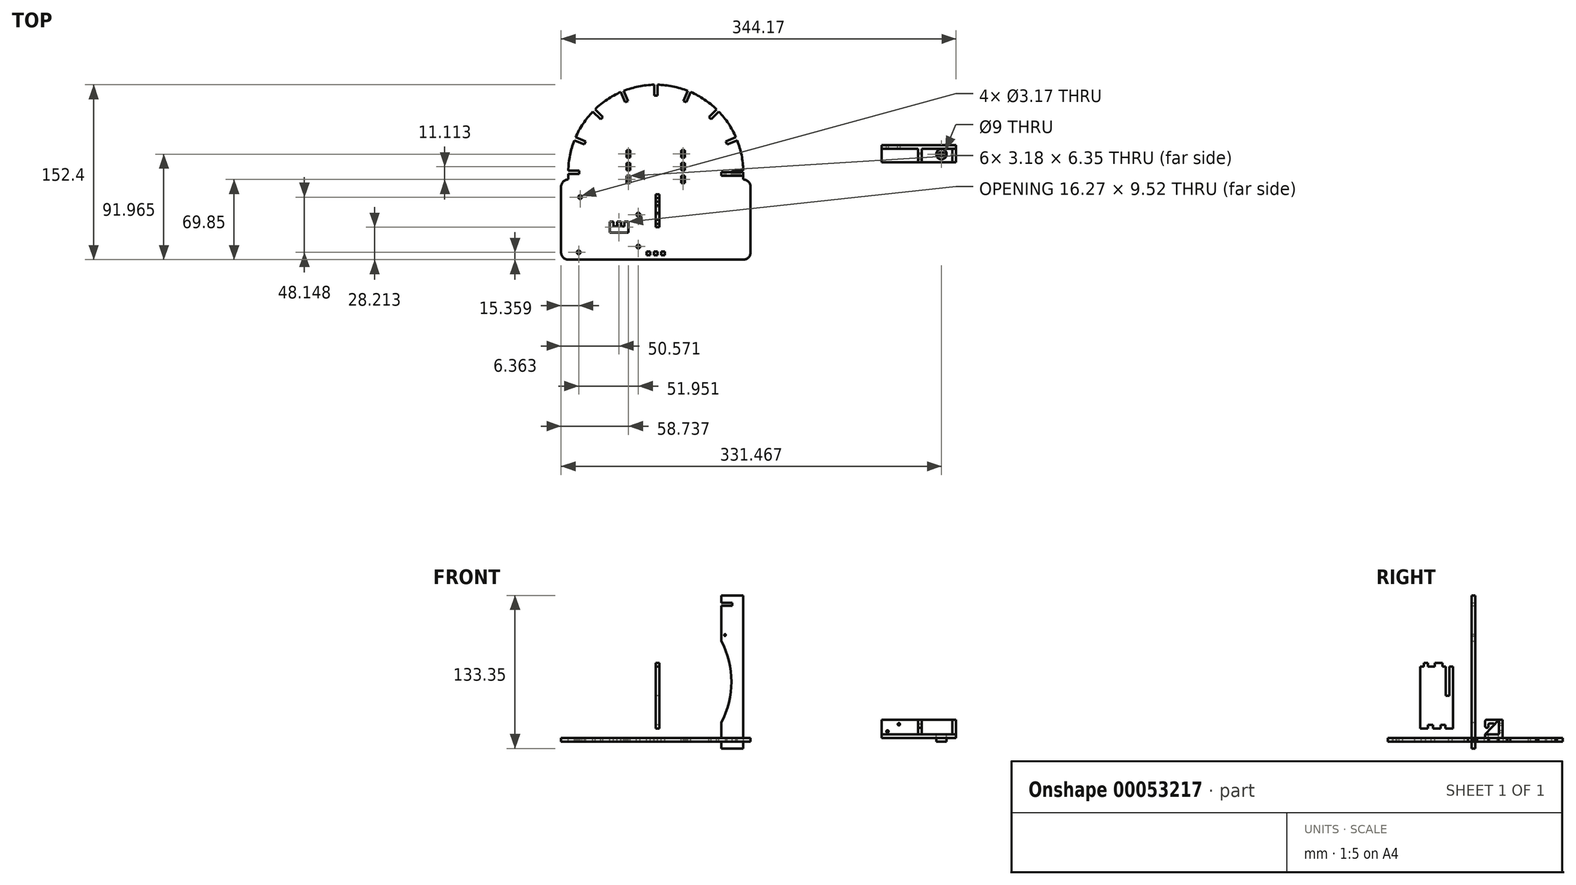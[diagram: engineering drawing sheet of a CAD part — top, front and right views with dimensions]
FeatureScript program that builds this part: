
annotation { "Feature Type Name" : "Feature", "Feature Type Description" : "" }
export const myFeature = defineFeature(function(context is Context, id is Id, definition is map)
    precondition{}
    {
        {
            var Q0;
            Q0=qCreatedBy(makeId("Top.planeOp"),FACE);
            var sketch = newSketch(context, id + "F0", { "sketchPlane" : qUnion([Q0])});
            skLineSegment(sketch, "E0", {"start": v(-76.2, -1.39) * mm, "end": v(-76.2, -6.35) * mm});
            skLineSegment(sketch, "E1", {"start": v(76.2, -1.39) * mm, "end": v(76.2, -6.35) * mm});
            skLineSegment(sketch, "E2.bottom", {"start": v(-66.67, -1.39) * mm, "end": v(-76.2, -1.39) * mm});
            skLineSegment(sketch, "E2.top", {"start": v(-66.67, 1.39) * mm, "end": v(-76.2, 1.39) * mm});
            skLineSegment(sketch, "E2.left", {"start": v(-66.67, -1.39) * mm, "end": v(-66.67, 1.39) * mm});
            skPoint(sketch, "E3", {"position": v(-76.2, 0) * mm});
            skLineSegment(sketch, "E4.1.0", {"start": v(-62.13, 24.23) * mm, "end": v(-70.93, 27.88) * mm});
            skLineSegment(sketch, "E4.1.1", {"start": v(-61.07, 26.8) * mm, "end": v(-69.87, 30.44) * mm});
            skLineSegment(sketch, "E4.1.2", {"start": v(-62.13, 24.23) * mm, "end": v(-61.07, 26.8) * mm});
            skLineSegment(sketch, "E4.2.0", {"start": v(-48.13, 46.16) * mm, "end": v(-54.86, 52.9) * mm});
            skLineSegment(sketch, "E4.2.1", {"start": v(-46.16, 48.13) * mm, "end": v(-52.9, 54.86) * mm});
            skLineSegment(sketch, "E4.2.2", {"start": v(-48.13, 46.16) * mm, "end": v(-46.16, 48.13) * mm});
            skLineSegment(sketch, "E4.3.0", {"start": v(-26.8, 61.07) * mm, "end": v(-30.44, 69.87) * mm});
            skLineSegment(sketch, "E4.3.1", {"start": v(-24.23, 62.13) * mm, "end": v(-27.88, 70.93) * mm});
            skLineSegment(sketch, "E4.3.2", {"start": v(-26.8, 61.07) * mm, "end": v(-24.23, 62.13) * mm});
            skLineSegment(sketch, "E4.4.0", {"start": v(-1.39, 66.67) * mm, "end": v(-1.39, 76.2) * mm});
            skLineSegment(sketch, "E4.4.1", {"start": v(1.39, 66.67) * mm, "end": v(1.39, 76.2) * mm});
            skLineSegment(sketch, "E4.4.2", {"start": v(-1.39, 66.67) * mm, "end": v(1.39, 66.67) * mm});
            skLineSegment(sketch, "E4.5.0", {"start": v(24.23, 62.13) * mm, "end": v(27.88, 70.93) * mm});
            skLineSegment(sketch, "E4.5.1", {"start": v(26.8, 61.07) * mm, "end": v(30.44, 69.87) * mm});
            skLineSegment(sketch, "E4.5.2", {"start": v(24.23, 62.13) * mm, "end": v(26.8, 61.07) * mm});
            skLineSegment(sketch, "E4.6.0", {"start": v(46.16, 48.13) * mm, "end": v(52.9, 54.86) * mm});
            skLineSegment(sketch, "E4.6.1", {"start": v(48.13, 46.16) * mm, "end": v(54.86, 52.9) * mm});
            skLineSegment(sketch, "E4.6.2", {"start": v(46.16, 48.13) * mm, "end": v(48.13, 46.16) * mm});
            skLineSegment(sketch, "E4.7.0", {"start": v(61.07, 26.8) * mm, "end": v(69.87, 30.44) * mm});
            skLineSegment(sketch, "E4.7.1", {"start": v(62.13, 24.23) * mm, "end": v(70.93, 27.88) * mm});
            skLineSegment(sketch, "E4.7.2", {"start": v(61.07, 26.8) * mm, "end": v(62.13, 24.23) * mm});
            skLineSegment(sketch, "E4.8.0", {"start": v(66.67, 1.39) * mm, "end": v(76.2, 1.39) * mm});
            skLineSegment(sketch, "E4.8.1", {"start": v(66.67, -1.39) * mm, "end": v(76.2, -1.39) * mm});
            skLineSegment(sketch, "E4.8.2", {"start": v(66.67, 1.39) * mm, "end": v(66.67, -1.39) * mm});
            skPoint(sketch, "E4.center", {"position": v(0, 0) * mm});
            skLineSegment(sketch, "E4.anchor1", {"start": v(0, 0) * mm, "end": v(-76.2, -1.39) * mm, "construction": true});
            skLineSegment(sketch, "E4.anchor2", {"start": v(0, 0) * mm, "end": v(76.2, 1.39) * mm, "construction": true});
            skPoint(sketch, "E5.orphan", {"position": v(76.2, 0) * mm});
            skArc(sketch, "E6", {"start": v(76.2, 1.39) * mm, "mid": v(74.75, 14.87) * mm, "end": v(70.93, 27.88) * mm});
            skLineSegment(sketch, "E7.trimOffspring", {"start": v(-76.2, -76.2) * mm, "end": v(76.2, -76.2) * mm});
            skLineSegment(sketch, "E8.bottom", {"start": v(-25.4, 19.05) * mm, "end": v(-22.23, 19.05) * mm});
            skLineSegment(sketch, "E8.top", {"start": v(-25.4, -9.53) * mm, "end": v(-22.23, -9.53) * mm});
            skLineSegment(sketch, "E8.left", {"start": v(-25.4, 19.05) * mm, "end": v(-25.4, 12.7) * mm});
            skLineSegment(sketch, "E8.right", {"start": v(-22.23, 19.05) * mm, "end": v(-22.23, 12.7) * mm});
            skLineSegment(sketch, "E9", {"start": v(-25.4, -9.53) * mm, "end": v(25.4, -9.53) * mm, "construction": true});
            skPoint(sketch, "E10", {"position": v(0, -9.53) * mm});
            skLineSegment(sketch, "E11", {"start": v(-25.4, 12.7) * mm, "end": v(-22.23, 12.7) * mm});
            skLineSegment(sketch, "E12", {"start": v(-25.4, -3.17) * mm, "end": v(-22.23, -3.18) * mm});
            skLineSegment(sketch, "E13", {"start": v(-25.4, 1.59) * mm, "end": v(-22.23, 1.59) * mm});
            skLineSegment(sketch, "E14", {"start": v(-25.4, 7.94) * mm, "end": v(-22.23, 7.94) * mm});
            skLineSegment(sketch, "E15.trimOffspring", {"start": v(-25.4, 7.94) * mm, "end": v(-25.4, 1.59) * mm});
            skLineSegment(sketch, "E16.trimOffspring", {"start": v(-22.23, 7.94) * mm, "end": v(-22.23, 1.59) * mm});
            skLineSegment(sketch, "E17.trimOffspring", {"start": v(-22.23, -3.18) * mm, "end": v(-22.23, -9.53) * mm});
            skLineSegment(sketch, "E18.trimOffspring", {"start": v(-25.4, -3.17) * mm, "end": v(-25.4, -9.53) * mm});
            skPoint(sketch, "E19", {"position": v(-25.4, 4.76) * mm});
            skLineSegment(sketch, "E20.MirrorCS", {"start": v(25.4, 7.94) * mm, "end": v(25.4, 1.59) * mm});
            skLineSegment(sketch, "E21.MirrorCS", {"start": v(25.4, 12.7) * mm, "end": v(22.23, 12.7) * mm});
            skLineSegment(sketch, "E22.MirrorCS", {"start": v(22.23, -3.18) * mm, "end": v(22.23, -9.53) * mm});
            skLineSegment(sketch, "E23.MirrorCS", {"start": v(25.4, -3.17) * mm, "end": v(25.4, -9.53) * mm});
            skLineSegment(sketch, "E24.MirrorCS", {"start": v(22.23, 7.94) * mm, "end": v(22.23, 1.59) * mm});
            skLineSegment(sketch, "E25.MirrorCS", {"start": v(25.4, 1.59) * mm, "end": v(22.23, 1.59) * mm});
            skLineSegment(sketch, "E26.MirrorCS", {"start": v(22.23, 19.05) * mm, "end": v(22.23, 12.7) * mm});
            skPoint(sketch, "E27.MirrorP", {"position": v(25.4, 4.76) * mm});
            skLineSegment(sketch, "E28.MirrorCS", {"start": v(25.4, 19.05) * mm, "end": v(25.4, 12.7) * mm});
            skLineSegment(sketch, "E29.MirrorCS", {"start": v(25.4, 7.94) * mm, "end": v(22.23, 7.94) * mm});
            skLineSegment(sketch, "E30.MirrorCS", {"start": v(25.4, 19.05) * mm, "end": v(22.23, 19.05) * mm});
            skLineSegment(sketch, "E31.MirrorCS", {"start": v(25.4, -9.52) * mm, "end": v(22.23, -9.53) * mm});
            skLineSegment(sketch, "E32.MirrorCS", {"start": v(25.4, -3.18) * mm, "end": v(22.23, -3.18) * mm});
            skArc(sketch, "E33.trimOffspring", {"start": v(-70.93, 27.88) * mm, "mid": v(-74.75, 14.87) * mm, "end": v(-76.2, 1.39) * mm});
            skArc(sketch, "E34.trimOffspring", {"start": v(-54.86, 52.9) * mm, "mid": v(-63.37, 42.34) * mm, "end": v(-69.87, 30.44) * mm});
            skArc(sketch, "E35.trimOffspring", {"start": v(-30.44, 69.87) * mm, "mid": v(-42.34, 63.37) * mm, "end": v(-52.9, 54.86) * mm});
            skArc(sketch, "E36.trimOffspring", {"start": v(-1.39, 76.2) * mm, "mid": v(-14.87, 74.75) * mm, "end": v(-27.88, 70.93) * mm});
            skArc(sketch, "E37.trimOffspring", {"start": v(27.88, 70.93) * mm, "mid": v(14.87, 74.75) * mm, "end": v(1.39, 76.2) * mm});
            skArc(sketch, "E38.trimOffspring", {"start": v(52.9, 54.86) * mm, "mid": v(42.34, 63.37) * mm, "end": v(30.44, 69.87) * mm});
            skArc(sketch, "E39.trimOffspring", {"start": v(69.87, 30.44) * mm, "mid": v(63.37, 42.34) * mm, "end": v(54.86, 52.9) * mm});
            skCircle(sketch, "E40", {"center": v(-15.24, -64.77) * mm, "radius": 1.59 * mm});
            skCircle(sketch, "E41", {"center": v(-67.2, -69.84) * mm, "radius": 1.59 * mm});
            skCircle(sketch, "E42", {"center": v(-65.92, -21.69) * mm, "radius": 1.59 * mm});
            skCircle(sketch, "E43", {"center": v(-15.24, -36.9) * mm, "radius": 1.59 * mm});
            skLineSegment(sketch, "E44.bottom", {"start": v(-1.59, -68.95) * mm, "end": v(1.59, -68.95) * mm});
            skLineSegment(sketch, "E44.top", {"start": v(-1.59, -72.12) * mm, "end": v(1.59, -72.12) * mm});
            skLineSegment(sketch, "E44.left", {"start": v(-1.59, -68.95) * mm, "end": v(-1.59, -72.12) * mm});
            skLineSegment(sketch, "E44.right", {"start": v(1.59, -68.95) * mm, "end": v(1.59, -72.12) * mm});
            skLineSegment(sketch, "E45.bottom", {"start": v(4.76, -68.95) * mm, "end": v(7.94, -68.95) * mm});
            skLineSegment(sketch, "E45.top", {"start": v(4.76, -72.12) * mm, "end": v(7.94, -72.12) * mm});
            skLineSegment(sketch, "E45.left", {"start": v(4.76, -68.95) * mm, "end": v(4.76, -72.12) * mm});
            skLineSegment(sketch, "E45.right", {"start": v(7.94, -68.95) * mm, "end": v(7.94, -72.12) * mm});
            skLineSegment(sketch, "E46.bottom", {"start": v(-4.76, -68.95) * mm, "end": v(-7.94, -68.95) * mm});
            skLineSegment(sketch, "E46.top", {"start": v(-4.76, -72.12) * mm, "end": v(-7.94, -72.12) * mm});
            skLineSegment(sketch, "E46.left", {"start": v(-4.76, -68.95) * mm, "end": v(-4.76, -72.12) * mm});
            skLineSegment(sketch, "E46.right", {"start": v(-7.94, -68.95) * mm, "end": v(-7.94, -72.12) * mm});
            skPoint(sketch, "E47", {"position": v(0, -72.12) * mm});
            skLineSegment(sketch, "E48.bottom", {"start": v(-40.11, -43.22) * mm, "end": v(-36.74, -43.22) * mm});
            skLineSegment(sketch, "E48.top", {"start": v(-40.11, -52.75) * mm, "end": v(-23.84, -52.75) * mm});
            skLineSegment(sketch, "E48.left", {"start": v(-40.11, -43.22) * mm, "end": v(-40.11, -52.75) * mm});
            skLineSegment(sketch, "E48.right", {"start": v(-23.84, -43.22) * mm, "end": v(-23.84, -52.75) * mm});
            skLineSegment(sketch, "E49", {"start": v(-36.74, -43.22) * mm, "end": v(-36.74, -47.08) * mm});
            skLineSegment(sketch, "E50", {"start": v(-36.74, -47.08) * mm, "end": v(-33.76, -47.08) * mm});
            skLineSegment(sketch, "E51", {"start": v(-33.76, -47.08) * mm, "end": v(-33.76, -43.22) * mm});
            skLineSegment(sketch, "E52", {"start": v(-30.2, -43.22) * mm, "end": v(-30.2, -47.08) * mm});
            skLineSegment(sketch, "E53", {"start": v(-30.2, -47.08) * mm, "end": v(-27.22, -47.08) * mm});
            skLineSegment(sketch, "E54", {"start": v(-27.22, -47.08) * mm, "end": v(-27.22, -43.22) * mm});
            skLineSegment(sketch, "E55.trimOffspring", {"start": v(-33.76, -43.22) * mm, "end": v(-30.2, -43.22) * mm});
            skLineSegment(sketch, "E56.trimOffspring", {"start": v(-27.22, -43.22) * mm, "end": v(-23.84, -43.22) * mm});
            skPoint(sketch, "E57", {"position": v(-31.98, -43.22) * mm});
            skPoint(sketch, "E58", {"position": v(-31.98, -52.75) * mm});
            skLineSegment(sketch, "E59", {"start": v(-76.2, -6.35) * mm, "end": v(-76.2, -6.35) * mm});
            skLineSegment(sketch, "E60", {"start": v(-82.55, -12.7) * mm, "end": v(-82.55, -69.85) * mm});
            skLineSegment(sketch, "E61", {"start": v(76.2, -6.35) * mm, "end": v(76.2, -6.35) * mm});
            skLineSegment(sketch, "E62", {"start": v(82.55, -12.7) * mm, "end": v(82.55, -69.85) * mm});
            skPoint(sketch, "E63.orphan", {"position": v(76.2, -76.2) * mm});
            skPoint(sketch, "E64.visualSharp", {"position": v(-82.55, -6.35) * mm});
            skArc(sketch, "E64.filletArc", {"start": v(-76.2, -6.35) * mm, "mid": v(-80.7, -8.2) * mm, "end": v(-82.55, -12.7) * mm});
            skPoint(sketch, "E65.visualSharp", {"position": v(82.55, -6.35) * mm});
            skArc(sketch, "E65.filletArc", {"start": v(82.55, -12.7) * mm, "mid": v(80.69, -8.2) * mm, "end": v(76.2, -6.35) * mm});
            skPoint(sketch, "E66.visualSharp", {"position": v(82.55, -76.2) * mm});
            skArc(sketch, "E66.filletArc", {"start": v(76.2, -76.2) * mm, "mid": v(80.69, -74.34) * mm, "end": v(82.55, -69.85) * mm});
            skPoint(sketch, "E67.visualSharp", {"position": v(-82.55, -76.2) * mm});
            skArc(sketch, "E67.filletArc", {"start": v(-82.55, -69.85) * mm, "mid": v(-80.7, -74.34) * mm, "end": v(-76.2, -76.2) * mm});
            skSolve(sketch);
        }
        {
            var Q0;
            Q0=makeQuery(id+"F0.imprint","IMPRINT",FACE,{"disambiguationData":[TD([[makeQuery(id+"F0.imprint","IMPRINT",EDGE,{"derivedFrom":sQuery(id+"F0.wireOp",EDGE,"E0")}),1.0]])]});
            extrude(context, id + "F1", {"entities" : qUnion([Q0]), "oppositeDirection" : true, "depth" : 3.17 * mm});
        }
        {
            var Q0;
            Q0=qCreatedBy(makeId("Front.planeOp"),FACE);
            var sketch = newSketch(context, id + "F2", { "sketchPlane" : qUnion([Q0])});
            skLineSegment(sketch, "E68.bottom", {"start": v(57.15, 124.22) * mm, "end": v(76.2, 124.22) * mm});
            skLineSegment(sketch, "E68.top", {"start": v(57.15, -9.13) * mm, "end": v(76.2, -9.13) * mm});
            skLineSegment(sketch, "E68.left", {"start": v(57.15, 124.22) * mm, "end": v(57.15, 117.87) * mm});
            skLineSegment(sketch, "E69", {"start": v(57.15, -2.78) * mm, "end": v(66.67, -2.78) * mm});
            skLineSegment(sketch, "E70", {"start": v(66.67, -2.78) * mm, "end": v(66.67, 0) * mm});
            skLineSegment(sketch, "E71", {"start": v(66.67, 0) * mm, "end": v(57.15, 0) * mm});
            skLineSegment(sketch, "E72.trimOffspring", {"start": v(76.2, 124.22) * mm, "end": v(76.2, -9.13) * mm});
            skLineSegment(sketch, "E73.trimOffspring", {"start": v(57.15, -2.78) * mm, "end": v(57.15, -9.13) * mm});
            skArc(sketch, "E74", {"start": v(57.15, 13.56) * mm, "mid": v(65.88, 48.98) * mm, "end": v(57.15, 84.4) * mm});
            skLineSegment(sketch, "E75.trimOffspring", {"start": v(57.15, 13.56) * mm, "end": v(57.15, 0) * mm});
            skCircle(sketch, "E76", {"center": v(60.32, 89.7) * mm, "radius": 0.75 * mm});
            skLineSegment(sketch, "E77", {"start": v(57.15, 117.87) * mm, "end": v(66.67, 117.87) * mm});
            skLineSegment(sketch, "E78", {"start": v(66.67, 117.87) * mm, "end": v(66.67, 115.1) * mm});
            skLineSegment(sketch, "E79", {"start": v(66.67, 115.1) * mm, "end": v(57.15, 115.1) * mm});
            skLineSegment(sketch, "E80.trimOffspring", {"start": v(57.15, 115.1) * mm, "end": v(57.15, 84.4) * mm});
            skSolve(sketch);
        }
        {
            var Q0;
            Q0=makeQuery(id+"F2.imprint","IMPRINT",FACE,{"disambiguationData":[TD([[makeQuery(id+"F2.imprint","IMPRINT",EDGE,{"derivedFrom":sQuery(id+"F2.wireOp",EDGE,"E68.bottom")}),-1.0]])]});
            extrude(context, id + "F3", {"entities" : qUnion([Q0]), "depth" : 3.17 * mm});
        }
        {
            var Q0;
            Q0=qCreatedBy(makeId("Right.planeOp"),FACE);
            var sketch = newSketch(context, id + "F4", { "sketchPlane" : qUnion([Q0])});
            skLineSegment(sketch, "E81.bottom", {"start": v(-41.23, 11.46) * mm, "end": v(-37.07, 11.46) * mm});
            skLineSegment(sketch, "E81.top", {"start": v(-41.43, 62.26) * mm, "end": v(-35.48, 62.26) * mm});
            skLineSegment(sketch, "E81.left", {"start": v(-47.98, 11.46) * mm, "end": v(-47.98, 62.26) * mm});
            skLineSegment(sketch, "E81.right", {"start": v(-19.4, 11.46) * mm, "end": v(-19.4, 62.26) * mm});
            skLineSegment(sketch, "E82", {"start": v(-22.58, 62.26) * mm, "end": v(-22.58, 36.86) * mm});
            skLineSegment(sketch, "E83", {"start": v(-22.58, 36.86) * mm, "end": v(-25.76, 36.86) * mm});
            skLineSegment(sketch, "E84", {"start": v(-25.76, 36.86) * mm, "end": v(-25.76, 62.26) * mm});
            skLineSegment(sketch, "E85", {"start": v(-47.98, 11.46) * mm, "end": v(-47.98, 8.29) * mm});
            skLineSegment(sketch, "E86", {"start": v(-47.98, 8.29) * mm, "end": v(-41.23, 8.29) * mm});
            skLineSegment(sketch, "E87", {"start": v(-41.23, 8.29) * mm, "end": v(-41.23, 11.46) * mm});
            skLineSegment(sketch, "E88", {"start": v(-19.4, 11.46) * mm, "end": v(-19.4, 8.29) * mm});
            skLineSegment(sketch, "E89", {"start": v(-30.32, 11.46) * mm, "end": v(-30.32, 8.29) * mm});
            skLineSegment(sketch, "E90", {"start": v(-30.32, 8.29) * mm, "end": v(-37.07, 8.29) * mm});
            skLineSegment(sketch, "E91", {"start": v(-37.07, 8.29) * mm, "end": v(-37.07, 11.46) * mm});
            skLineSegment(sketch, "E92", {"start": v(-19.4, 8.29) * mm, "end": v(-26.15, 8.29) * mm});
            skLineSegment(sketch, "E93", {"start": v(-26.15, 8.29) * mm, "end": v(-26.15, 11.46) * mm});
            skLineSegment(sketch, "E94.trimOffspring", {"start": v(-22.58, 62.26) * mm, "end": v(-19.4, 62.26) * mm});
            skLineSegment(sketch, "E95.trimOffspring", {"start": v(-30.32, 11.46) * mm, "end": v(-26.15, 11.46) * mm});
            skLineSegment(sketch, "E96", {"start": v(-45, 65.44) * mm, "end": v(-41.43, 65.44) * mm});
            skLineSegment(sketch, "E97", {"start": v(-41.43, 65.44) * mm, "end": v(-41.43, 62.26) * mm});
            skLineSegment(sketch, "E98", {"start": v(-28.73, 62.26) * mm, "end": v(-28.73, 65.44) * mm});
            skLineSegment(sketch, "E99", {"start": v(-28.73, 65.44) * mm, "end": v(-35.48, 65.44) * mm});
            skLineSegment(sketch, "E100", {"start": v(-35.48, 65.44) * mm, "end": v(-35.48, 62.26) * mm});
            skLineSegment(sketch, "E101.trimOffspring", {"start": v(-28.73, 62.26) * mm, "end": v(-25.76, 62.26) * mm});
            skLineSegment(sketch, "E102", {"start": v(-45, 65.44) * mm, "end": v(-45, 62.26) * mm});
            skLineSegment(sketch, "E103", {"start": v(-45, 62.26) * mm, "end": v(-47.98, 62.26) * mm});
            skPoint(sketch, "E104", {"position": v(-43.22, 65.44) * mm});
            skPoint(sketch, "E105", {"position": v(-32.1, 65.44) * mm});
            skLineSegment(sketch, "E106", {"start": v(-47.98, 16.7) * mm, "end": v(-19.4, 16.7) * mm, "construction": true});
            skPoint(sketch, "E107", {"position": v(-33.7, 8.29) * mm});
            skPoint(sketch, "E108", {"position": v(-33.7, 16.7) * mm});
            skSolve(sketch);
        }
        {
            var Q0;
            Q0=makeQuery(id+"F4.imprint","IMPRINT",FACE,{"disambiguationData":[TD([[makeQuery(id+"F4.imprint","IMPRINT",EDGE,{"derivedFrom":sQuery(id+"F4.wireOp",EDGE,"E81.bottom")}),1.0]])]});
            extrude(context, id + "F5", {"entities" : qUnion([Q0]), "depth" : 3.17 * mm});
        }
        {
            var Q0;
            Q0=qCreatedBy(makeId("Top.planeOp"),FACE);
            var sketch = newSketch(context, id + "F6", { "sketchPlane" : qUnion([Q0])});
            skPoint(sketch, "E109", {"position": v(248.92, 15.77) * mm});
            skCircle(sketch, "E110", {"center": v(248.92, 15.77) * mm, "radius": 4.5 * mm});
            skLineSegment(sketch, "E111.bottom", {"start": v(247.04, 17.42) * mm, "end": v(250.8, 17.42) * mm});
            skLineSegment(sketch, "E111.top", {"start": v(247.04, 14.12) * mm, "end": v(250.8, 14.12) * mm});
            skCircle(sketch, "E112", {"center": v(248.92, 15.77) * mm, "radius": 2.5 * mm});
            skLineSegment(sketch, "E113.bottom", {"start": v(261.62, 8.58) * mm, "end": v(196.85, 8.58) * mm});
            skLineSegment(sketch, "E113.top", {"start": v(261.62, 23.58) * mm, "end": v(196.85, 23.58) * mm});
            skLineSegment(sketch, "E113.left", {"start": v(261.62, 8.58) * mm, "end": v(261.62, 23.58) * mm});
            skLineSegment(sketch, "E113.right", {"start": v(196.85, 8.58) * mm, "end": v(196.85, 23.58) * mm});
            skSolve(sketch);
        }
        {
            var Q0;
            {var subQ0=sQuery(id+"F6.wireOp",EDGE,"E111.bottom");Q0=makeQuery(id+"F6.imprint","IMPRINT",FACE,{"disambiguationData":[TD([[makeQuery(id+"F6.imprint","IMPRINT",EDGE,{"derivedFrom":subQ0}),1.0]])]});}
            var Q1;
            {var subQ0=sQuery(id+"F6.wireOp",EDGE,"E111.top");Q1=makeQuery(id+"F6.imprint","IMPRINT",FACE,{"disambiguationData":[TD([[makeQuery(id+"F6.imprint","IMPRINT",EDGE,{"derivedFrom":subQ0}),-1.0]])]});}
            var Q2;
            Q2=makeQuery(id+"F6.imprint","IMPRINT",FACE,{"disambiguationData":[TD([[makeQuery(id+"F6.imprint","IMPRINT",EDGE,{"derivedFrom":sQuery(id+"F6.wireOp",EDGE,"E110")}),1.0]])]});
            extrude(context, id + "F7", {"entities" : qUnion([Q0, Q1, Q2]), "endBound" : BoundingType.SYMMETRIC, "oppositeDirection" : true, "depth" : 6.35 * mm});
        }
        {
            var Q0;
            Q0 = qSketchRegion(id + "F6", true);
            extrude(context, id + "F8", {"entities" : qUnion([Q0]), "depth" : 3.17 * mm});
        }
        {
            var Q0;
            Q0=makeQuery(id+"F8.opExtrude","CAP_FACE",FACE,{"disambiguationData":[OSD([sQuery(id+"F6.wireOp",EDGE,"E110"),sQuery(id+"F6.wireOp",EDGE,"E113.bottom"),sQuery(id+"F6.wireOp",EDGE,"E113.top"),sQuery(id+"F6.wireOp",EDGE,"E113.left"),sQuery(id+"F6.wireOp",EDGE,"E113.right")])],"isStart":false});
            var sketch = newSketch(context, id + "F9", { "sketchPlane" : qUnion([Q0])});
            skLineSegment(sketch, "E114.bottom", {"start": v(196.85, 23.58) * mm, "end": v(261.62, 23.58) * mm});
            skLineSegment(sketch, "E114.top", {"start": v(196.85, 20.4) * mm, "end": v(261.62, 20.4) * mm});
            skLineSegment(sketch, "E114.left", {"start": v(196.85, 23.58) * mm, "end": v(196.85, 20.4) * mm});
            skLineSegment(sketch, "E114.right", {"start": v(261.62, 23.58) * mm, "end": v(261.62, 20.4) * mm});
            skSolve(sketch);
        }
        {
            var Q0;
            Q0=makeQuery(id+"F9.imprint","IMPRINT",FACE,{"disambiguationData":[TD([[makeQuery(id+"F9.imprint","IMPRINT",EDGE,{"derivedFrom":sQuery(id+"F9.wireOp",EDGE,"E114.bottom")}),1.0]])]});
            extrude(context, id + "F10", {"entities" : qUnion([Q0]), "operationType" : NewBodyOperationType.ADD, "depth" : 12.7 * mm});
        }
        {
            var Q0;
            Q0=makeQuery(id+"F10.boolean.opBoolean","MERGE",FACE,{"derivedFrom":[makeQuery(id+"F8.opExtrude","SWEPT_FACE",FACE,{"disambiguationData":[OSD([sQuery(id+"F6.wireOp",EDGE,"E113.left")])]}),makeQuery(id+"F10.opExtrude","SWEPT_FACE",FACE,{"disambiguationData":[OSD([sQuery(id+"F9.wireOp",EDGE,"E114.right")])]})]});
            var sketch = newSketch(context, id + "F11", { "sketchPlane" : qUnion([Q0])});
            skLineSegment(sketch, "E115", {"start": v(8.58, 3.17) * mm, "end": v(20.4, 15.88) * mm});
            skSolve(sketch);
        }
        {
            var Q0;
            Q0 = qSketchRegion(id + "F11", true);
            var Q1;
            Q1=makeQuery(id+"F11.imprint","IMPRINT",FACE,{"disambiguationData":[TD([[makeQuery(id+"F11.imprint","IMPRINT",EDGE,{"derivedFrom":sQuery(id+"F11.wireOp",EDGE,"E115")}),-1.0]])]});
            extrude(context, id + "F12", {"entities" : qUnion([Q0, Q1]), "oppositeDirection" : true, "depth" : 3.17 * mm});
        }
        {
            var Q0;
            Q0=makeQuery(id+"F8.opExtrude","CAP_FACE",FACE,{"disambiguationData":[OSD([sQuery(id+"F6.wireOp",EDGE,"E110"),sQuery(id+"F6.wireOp",EDGE,"E113.bottom"),sQuery(id+"F6.wireOp",EDGE,"E113.top"),sQuery(id+"F6.wireOp",EDGE,"E113.left"),sQuery(id+"F6.wireOp",EDGE,"E113.right")])],"isStart":false});
            var sketch = newSketch(context, id + "F13", { "sketchPlane" : qUnion([Q0])});
            skLineSegment(sketch, "E116", {"start": v(228.6, 20.4) * mm, "end": v(228.6, 8.58) * mm});
            skLineSegment(sketch, "E117", {"start": v(231.77, 20.4) * mm, "end": v(231.77, 8.58) * mm});
            skSolve(sketch);
        }
        {
            var Q0;
            Q0 = qSketchRegion(id + "F13", true);
            var Q1;
            {var subQ0=sQuery(id+"F13.wireOp",EDGE,"E116");Q1=makeQuery(id+"F13.imprint","IMPRINT",FACE,{"disambiguationData":[TD([[makeQuery(id+"F13.imprint","IMPRINT",EDGE,{"derivedFrom":subQ0}),1.0]])]});}
            extrude(context, id + "F14", {"entities" : qUnion([Q0, Q1]), "operationType" : NewBodyOperationType.ADD, "depth" : 12.7 * mm});
        }
        {
            var Q0;
            Q0=makeQuery(id+"F14.opExtrude","SWEPT_FACE",FACE,{"disambiguationData":[OSD([sQuery(id+"F13.wireOp",EDGE,"E117")])]});
            var sketch = newSketch(context, id + "F15", { "sketchPlane" : qUnion([Q0])});
            skLineSegment(sketch, "E118", {"start": v(16.84, 12.04) * mm, "end": v(8.58, 3.18) * mm});
            skLineSegment(sketch, "E119", {"start": v(9.8, 8.89) * mm, "end": v(10.14, 8.89) * mm});
            skLineSegment(sketch, "E120", {"start": v(11.34, 10.1) * mm, "end": v(11.34, 11.5) * mm});
            skLineSegment(sketch, "E121", {"start": v(12.55, 12.7) * mm, "end": v(16.14, 12.7) * mm});
            skPoint(sketch, "E122.visualSharp", {"position": v(11.34, 8.89) * mm});
            skArc(sketch, "E122.filletArc", {"start": v(10.14, 8.89) * mm, "mid": v(11, 9.24) * mm, "end": v(11.34, 10.1) * mm});
            skPoint(sketch, "E123.visualSharp", {"position": v(11.34, 12.7) * mm});
            skArc(sketch, "E123.filletArc", {"start": v(12.55, 12.7) * mm, "mid": v(11.7, 12.35) * mm, "end": v(11.34, 11.5) * mm});
            skLineSegment(sketch, "E124", {"start": v(8.58, 10.1) * mm, "end": v(8.58, 14.67) * mm});
            skLineSegment(sketch, "E125", {"start": v(9.8, 15.88) * mm, "end": v(20.4, 15.88) * mm});
            skPoint(sketch, "E126.visualSharp", {"position": v(8.58, 15.88) * mm});
            skArc(sketch, "E126.filletArc", {"start": v(9.8, 15.88) * mm, "mid": v(8.94, 15.52) * mm, "end": v(8.58, 14.67) * mm});
            skPoint(sketch, "E127.visualSharp", {"position": v(8.58, 8.89) * mm});
            skArc(sketch, "E127.filletArc", {"start": v(8.58, 10.1) * mm, "mid": v(8.94, 9.24) * mm, "end": v(9.8, 8.89) * mm});
            skLineSegment(sketch, "E128", {"start": v(16.14, 12.7) * mm, "end": v(16.84, 12.04) * mm});
            skSolve(sketch);
        }
        {
            var Q0;
            Q0 = qSketchRegion(id + "F15", true);
            var Q1;
            Q1=makeQuery(id+"F15.imprint","IMPRINT",FACE,{"disambiguationData":[TD([[makeQuery(id+"F15.imprint","IMPRINT",EDGE,{"derivedFrom":sQuery(id+"F15.wireOp",EDGE,"E118")}),-1.0]])]});
            var Q2;
            {var subQ0=sQuery(id+"F15.wireOp",EDGE,"E126.filletArc");Q2=makeQuery(id+"F15.imprint","IMPRINT",FACE,{"disambiguationData":[TD([[makeQuery(id+"F15.imprint","IMPRINT",EDGE,{"derivedFrom":subQ0}),-1.0]])]});}
            extrude(context, id + "F16", {"entities" : qUnion([Q0, Q1, Q2]), "operationType" : NewBodyOperationType.REMOVE, "oppositeDirection" : true, "depth" : 7.67 * mm});
        }
        {
            var Q0;
            Q0=makeQuery(id+"F10.boolean.opBoolean","MERGE",FACE,{"derivedFrom":[makeQuery(id+"F8.opExtrude","SWEPT_FACE",FACE,{"disambiguationData":[OSD([sQuery(id+"F6.wireOp",EDGE,"E113.top")])]}),makeQuery(id+"F10.opExtrude","SWEPT_FACE",FACE,{"disambiguationData":[OSD([sQuery(id+"F9.wireOp",EDGE,"E114.bottom")])]})]});
            var sketch = newSketch(context, id + "F17", { "sketchPlane" : qUnion([Q0])});
            skLineSegment(sketch, "E129", {"start": v(-196.85, 3.18) * mm, "end": v(-261.62, 3.17) * mm, "construction": true});
            skCircle(sketch, "E130", {"center": v(-201.85, 5.68) * mm, "radius": 1 * mm});
            skCircle(sketch, "E131", {"center": v(-211.85, 11.92) * mm, "radius": 1 * mm});
            skSolve(sketch);
        }
        {
            var Q0;
            Q0 = qSketchRegion(id + "F17", true);
            extrude(context, id + "F18", {"entities" : qUnion([Q0]), "operationType" : NewBodyOperationType.REMOVE, "oppositeDirection" : true, "depth" : 12.7 * mm});
        }
    });
